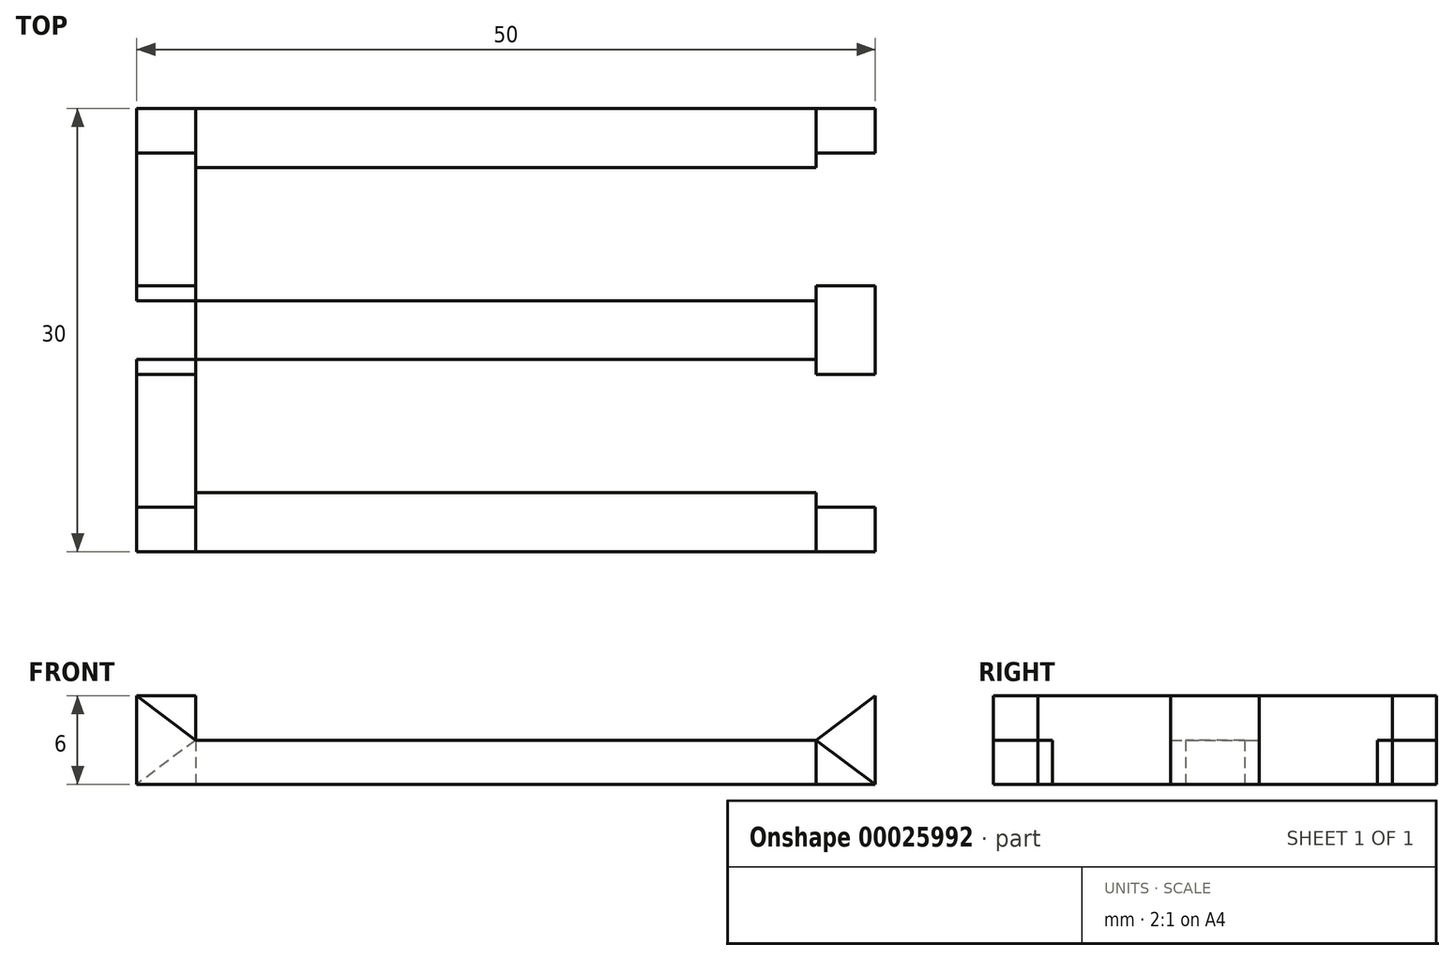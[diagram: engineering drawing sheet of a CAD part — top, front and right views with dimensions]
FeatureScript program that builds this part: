
annotation { "Feature Type Name" : "Feature", "Feature Type Description" : "" }
export const myFeature = defineFeature(function(context is Context, id is Id, definition is map)
    precondition{}
    {
        {
            var Q0;
            Q0=qCreatedBy(makeId("Top.planeOp"),FACE);
            cPlane(context, id + "F0", {"entities" : qUnion([Q0]), "cplaneType" : CPlaneType.OFFSET, "offset" : 3 * mm, "oppositeDirection" : true, "width" : 150 * mm, "height" : 150 * mm});
        }
        {
            var Q0;
            Q0=qCreatedBy(makeId("Top.planeOp"),FACE);
            var sketch = newSketch(context, id + "F1", { "sketchPlane" : qUnion([Q0])});
            skLineSegment(sketch, "E0", {"start": v(0, 0) * mm, "end": v(0, -19.58) * mm});
            skSolve(sketch);
        }
        {
            var Q0;
            Q0=qCreatedBy(id+"F0.planeOp",FACE);
            var sketch = newSketch(context, id + "F2", { "sketchPlane" : qUnion([Q0])});
            skLineSegment(sketch, "E1.rect.bottom", {"start": v(25, 15) * mm, "end": v(-25, 15) * mm});
            skLineSegment(sketch, "E1.rect.top", {"start": v(25, -15) * mm, "end": v(-25, -15) * mm});
            skLineSegment(sketch, "E1.rect.left", {"start": v(25, 15) * mm, "end": v(25, -15) * mm});
            skLineSegment(sketch, "E1.rect.right", {"start": v(-25, 15) * mm, "end": v(-25, -15) * mm});
            skPoint(sketch, "E1.rect.middle", {"position": v(0, 0) * mm});
            skLineSegment(sketch, "E2.0", {"start": v(25, 11) * mm, "end": v(-25, 11) * mm});
            skLineSegment(sketch, "E3.0", {"start": v(25, -11) * mm, "end": v(-25, -11) * mm});
            skLineSegment(sketch, "E4.0", {"start": v(-21, 15) * mm, "end": v(-21, -15) * mm});
            skLineSegment(sketch, "E5.0", {"start": v(21, 15) * mm, "end": v(21, -15) * mm});
            skLineSegment(sketch, "E6.rect.bottom", {"start": v(-25, 2) * mm, "end": v(25, 2) * mm});
            skLineSegment(sketch, "E6.rect.top", {"start": v(-25, -2) * mm, "end": v(25, -2) * mm});
            skLineSegment(sketch, "E6.rect.left", {"start": v(-25, 2) * mm, "end": v(-25, -2) * mm});
            skLineSegment(sketch, "E6.rect.right", {"start": v(25, 2) * mm, "end": v(25, -2) * mm});
            skSolve(sketch);
        }
        {
            var Q0;
            {var subQ3=sQuery(id+"F2.wireOp",EDGE,"E1.rect.right");var subQ6=sQuery(id+"F2.wireOp",EDGE,"E1.rect.top");var subQ8=makeQuery(id+"F2.imprint","INTERSECT",VERTEX,{"derivedFrom":[subQ6,subQ3]});Q0=makeQuery(id+"F2.imprint","IMPRINT",FACE,{"disambiguationData":[TD([[makeQuery(id+"F2.imprint","IMPRINT",EDGE,{"disambiguationData":[TD([[subQ8,1.0]])],"derivedFrom":subQ6}),-1.0]])]});}
            var Q1;
            {var subQ3=sQuery(id+"F2.wireOp",EDGE,"E1.rect.top");var subQ5=sQuery(id+"F2.wireOp",EDGE,"E4.0");var subQ7=makeQuery(id+"F2.imprint","INTERSECT",VERTEX,{"derivedFrom":[subQ3,subQ5]});Q1=makeQuery(id+"F2.imprint","IMPRINT",FACE,{"disambiguationData":[TD([[makeQuery(id+"F2.imprint","IMPRINT",EDGE,{"disambiguationData":[TD([[subQ7,1.0]])],"derivedFrom":subQ3}),-1.0]])]});}
            var Q2;
            {var subQ0=sQuery(id+"F2.wireOp",EDGE,"E6.rect.left");Q2=makeQuery(id+"F2.imprint","IMPRINT",FACE,{"disambiguationData":[TD([[makeQuery(id+"F2.imprint","IMPRINT",EDGE,{"derivedFrom":subQ0}),1.0]])]});}
            var Q3;
            {var subQ4=sQuery(id+"F2.wireOp",EDGE,"E1.rect.bottom");var subQ6=sQuery(id+"F2.wireOp",EDGE,"E1.rect.right");var subQ8=makeQuery(id+"F2.imprint","INTERSECT",VERTEX,{"derivedFrom":[subQ4,subQ6]});Q3=makeQuery(id+"F2.imprint","IMPRINT",FACE,{"disambiguationData":[TD([[makeQuery(id+"F2.imprint","IMPRINT",EDGE,{"disambiguationData":[TD([[subQ8,1.0]])],"derivedFrom":subQ4}),1.0]])]});}
            var Q4;
            {var subQ0=sQuery(id+"F2.wireOp",EDGE,"E4.0");var subQ3=sQuery(id+"F2.wireOp",EDGE,"E1.rect.bottom");var subQ4=makeQuery(id+"F2.imprint","INTERSECT",VERTEX,{"derivedFrom":[subQ3,subQ0]});Q4=makeQuery(id+"F2.imprint","IMPRINT",FACE,{"disambiguationData":[TD([[makeQuery(id+"F2.imprint","IMPRINT",EDGE,{"disambiguationData":[TD([[subQ4,1.0]])],"derivedFrom":subQ3}),1.0]])]});}
            var Q5;
            {var subQ3=sQuery(id+"F2.wireOp",EDGE,"E4.0");var subQ5=sQuery(id+"F2.wireOp",EDGE,"E6.rect.bottom");var subQ7=makeQuery(id+"F2.imprint","INTERSECT",VERTEX,{"derivedFrom":[subQ3,subQ5]});Q5=makeQuery(id+"F2.imprint","IMPRINT",FACE,{"disambiguationData":[TD([[makeQuery(id+"F2.imprint","IMPRINT",EDGE,{"disambiguationData":[TD([[subQ7,-1.0]])],"derivedFrom":subQ3}),1.0]])]});}
            var Q6;
            {var subQ3=sQuery(id+"F2.wireOp",EDGE,"E1.rect.right");var subQ5=sQuery(id+"F2.wireOp",EDGE,"E2.0");var subQ7=makeQuery(id+"F2.imprint","INTERSECT",VERTEX,{"derivedFrom":[subQ3,subQ5]});Q6=makeQuery(id+"F2.imprint","IMPRINT",FACE,{"disambiguationData":[TD([[makeQuery(id+"F2.imprint","IMPRINT",EDGE,{"disambiguationData":[TD([[subQ7,1.0]])],"derivedFrom":subQ5}),1.0]])]});}
            var Q7;
            {var subQ3=sQuery(id+"F2.wireOp",EDGE,"E1.rect.right");var subQ5=sQuery(id+"F2.wireOp",EDGE,"E3.0");var subQ7=makeQuery(id+"F2.imprint","INTERSECT",VERTEX,{"derivedFrom":[subQ3,subQ5]});Q7=makeQuery(id+"F2.imprint","IMPRINT",FACE,{"disambiguationData":[TD([[makeQuery(id+"F2.imprint","IMPRINT",EDGE,{"disambiguationData":[TD([[subQ7,1.0]])],"derivedFrom":subQ5}),-1.0]])]});}
            extrude(context, id + "F3", {"entities" : qUnion([Q0, Q1, Q2, Q3, Q4, Q5, Q6, Q7]), "depth" : 3 * mm});
        }
        {
            var Q0;
            {var subQ3=sQuery(id+"F2.wireOp",EDGE,"E1.rect.bottom");var subQ5=sQuery(id+"F2.wireOp",EDGE,"E1.rect.right");var subQ7=makeQuery(id+"F2.imprint","INTERSECT",VERTEX,{"derivedFrom":[subQ3,subQ5]});Q0=makeQuery(id+"F2.imprint","IMPRINT",FACE,{"disambiguationData":[TD([[makeQuery(id+"F2.imprint","IMPRINT",EDGE,{"disambiguationData":[TD([[subQ7,1.0]])],"derivedFrom":subQ3}),1.0]])]});}
            var Q1;
            {var subQ3=sQuery(id+"F2.wireOp",EDGE,"E1.rect.top");var subQ5=sQuery(id+"F2.wireOp",EDGE,"E1.rect.right");var subQ7=makeQuery(id+"F2.imprint","INTERSECT",VERTEX,{"derivedFrom":[subQ3,subQ5]});Q1=makeQuery(id+"F2.imprint","IMPRINT",FACE,{"disambiguationData":[TD([[makeQuery(id+"F2.imprint","IMPRINT",EDGE,{"disambiguationData":[TD([[subQ7,1.0]])],"derivedFrom":subQ3}),-1.0]])]});}
            var Q2;
            {var subQ3=sQuery(id+"F2.wireOp",EDGE,"E1.rect.right");var subQ5=sQuery(id+"F2.wireOp",EDGE,"E2.0");var subQ7=makeQuery(id+"F2.imprint","INTERSECT",VERTEX,{"derivedFrom":[subQ3,subQ5]});Q2=makeQuery(id+"F2.imprint","IMPRINT",FACE,{"disambiguationData":[TD([[makeQuery(id+"F2.imprint","IMPRINT",EDGE,{"disambiguationData":[TD([[subQ7,1.0]])],"derivedFrom":subQ5}),1.0]])]});}
            var Q3;
            {var subQ3=sQuery(id+"F2.wireOp",EDGE,"E1.rect.right");var subQ5=sQuery(id+"F2.wireOp",EDGE,"E3.0");var subQ7=makeQuery(id+"F2.imprint","INTERSECT",VERTEX,{"derivedFrom":[subQ3,subQ5]});Q3=makeQuery(id+"F2.imprint","IMPRINT",FACE,{"disambiguationData":[TD([[makeQuery(id+"F2.imprint","IMPRINT",EDGE,{"disambiguationData":[TD([[subQ7,1.0]])],"derivedFrom":subQ5}),-1.0]])]});}
            extrude(context, id + "F4", {"entities" : qUnion([Q0, Q1, Q2, Q3]), "operationType" : NewBodyOperationType.ADD, "depth" : 6 * mm});
        }
        {
            var Q0;
            Q0=qCreatedBy(makeId("Front.planeOp"),FACE);
            var sketch = newSketch(context, id + "F5", { "sketchPlane" : qUnion([Q0])});
            skLineSegment(sketch, "E7.bottom", {"start": v(25, -3) * mm, "end": v(21, -3) * mm});
            skLineSegment(sketch, "E7.top", {"start": v(25, 3) * mm, "end": v(21, 3) * mm});
            skLineSegment(sketch, "E7.left", {"start": v(25, -3) * mm, "end": v(25, 3) * mm});
            skLineSegment(sketch, "E7.right", {"start": v(21, -3) * mm, "end": v(21, 3) * mm});
            skLineSegment(sketch, "E8", {"start": v(21, 0) * mm, "end": v(25, 3) * mm});
            skSolve(sketch);
        }
        {
            var Q0;
            {var subQ2=sQuery(id+"F5.wireOp",EDGE,"E7.bottom");Q0=makeQuery(id+"F5.imprint","IMPRINT",FACE,{"disambiguationData":[TD([[makeQuery(id+"F5.imprint","IMPRINT",EDGE,{"derivedFrom":subQ2}),-1.0]])]});}
            extrude(context, id + "F6", {"entities" : qUnion([Q0]), "depth" : 3 * mm, "hasSecondDirection" : true, "secondDirectionOppositeDirection" : true, "secondDirectionDepth" : 3 * mm});
        }
        {
            var Q0;
            Q0=makeQuery(id+"F3.opExtrude","SWEPT_FACE",FACE,{"disambiguationData":[OSD([sQuery(id+"F2.wireOp",EDGE,"E1.rect.top")])]});
            var sketch = newSketch(context, id + "F7", { "sketchPlane" : qUnion([Q0])});
            skLineSegment(sketch, "E9", {"start": v(21, 0) * mm, "end": v(25, -3) * mm});
            skPoint(sketch, "E10.0", {"position": v(21, 0) * mm});
            skLineSegment(sketch, "E11", {"start": v(21, 0) * mm, "end": v(21, 0) * mm});
            skPoint(sketch, "E12.0", {"position": v(25, -3) * mm});
            skLineSegment(sketch, "E13", {"start": v(21, -3) * mm, "end": v(21, 0) * mm});
            skLineSegment(sketch, "E14", {"start": v(21, -3) * mm, "end": v(25, -3) * mm});
            skSolve(sketch);
        }
        {
            var Q0;
            Q0=makeQuery(id+"F7.imprint","IMPRINT",FACE,{"disambiguationData":[TD([[makeQuery(id+"F7.imprint","IMPRINT",EDGE,{"derivedFrom":sQuery(id+"F7.wireOp",EDGE,"E9")}),-1.0]])]});
            extrude(context, id + "F8", {"entities" : qUnion([Q0]), "oppositeDirection" : true, "depth" : 3 * mm});
        }
        {
            var Q0;
            Q0=makeQuery(id+"F3.opExtrude","SWEPT_FACE",FACE,{"disambiguationData":[OSD([sQuery(id+"F2.wireOp",EDGE,"E1.rect.bottom")])]});
            var sketch = newSketch(context, id + "F9", { "sketchPlane" : qUnion([Q0])});
            skPoint(sketch, "E15.0", {"position": v(-25, -3) * mm});
            skPoint(sketch, "E15.1", {"position": v(-21, 0) * mm});
            skPoint(sketch, "E15.2", {"position": v(-21, 0) * mm});
            skLineSegment(sketch, "E16.4", {"start": v(-21, 0) * mm, "end": v(-25, -3) * mm});
            skLineSegment(sketch, "E17", {"start": v(-21, -3) * mm, "end": v(-25, -3) * mm});
            skLineSegment(sketch, "E18", {"start": v(-21, -3) * mm, "end": v(-21, 0) * mm});
            skSolve(sketch);
        }
        {
            var Q0;
            Q0=makeQuery(id+"F9.imprint","IMPRINT",FACE,{"disambiguationData":[TD([[makeQuery(id+"F9.imprint","IMPRINT",EDGE,{"derivedFrom":sQuery(id+"F9.wireOp",EDGE,"E16.4")}),1.0]])]});
            extrude(context, id + "F10", {"entities" : qUnion([Q0]), "oppositeDirection" : true, "depth" : 3 * mm});
        }
        {
            var Q0;
            Q0=makeQuery(id+"F6.opExtrude","SWEPT_BODY",BODY,{"disambiguationData":[OSD([sQuery(id+"F5.wireOp",EDGE,"E7.bottom"),sQuery(id+"F5.wireOp",EDGE,"E7.left"),sQuery(id+"F5.wireOp",EDGE,"E7.right"),sQuery(id+"F5.wireOp",EDGE,"E8")])]});
            var Q1;
            Q1=makeQuery(id+"F8.opExtrude","SWEPT_BODY",BODY,{"disambiguationData":[OSD([sQuery(id+"F7.wireOp",EDGE,"E9"),sQuery(id+"F7.wireOp",EDGE,"E13"),sQuery(id+"F7.wireOp",EDGE,"E14")])]});
            var Q2;
            Q2=makeQuery(id+"F10.opExtrude","SWEPT_BODY",BODY,{"disambiguationData":[OSD([sQuery(id+"F9.wireOp",EDGE,"E16.4"),sQuery(id+"F9.wireOp",EDGE,"E17"),sQuery(id+"F9.wireOp",EDGE,"E18")])]});
            var Q3;
            Q3=sQuery(id+"F1.wireOp",EDGE,"E0");
            transform(context, id + "F11", {"entities" : qUnion([Q0, Q1, Q2]), "transformType" : TransformType.ROTATION, "transformAxis" : qUnion([Q3]), "angle" : 180 * degree, "makeCopy" : true});
        }
        {
            var Q0;
            Q0=makeQuery(id+"F11.opPattern","COPY",BODY,{"derivedFrom":makeQuery(id+"F6.opExtrude","SWEPT_BODY",BODY,{"disambiguationData":[OSD([sQuery(id+"F5.wireOp",EDGE,"E7.bottom"),sQuery(id+"F5.wireOp",EDGE,"E7.left"),sQuery(id+"F5.wireOp",EDGE,"E7.right"),sQuery(id+"F5.wireOp",EDGE,"E8")])]}),"instanceName":"1"});
            var Q1;
            Q1=makeQuery(id+"F11.opPattern","COPY",BODY,{"derivedFrom":makeQuery(id+"F8.opExtrude","SWEPT_BODY",BODY,{"disambiguationData":[OSD([sQuery(id+"F7.wireOp",EDGE,"E9"),sQuery(id+"F7.wireOp",EDGE,"E13"),sQuery(id+"F7.wireOp",EDGE,"E14")])]}),"instanceName":"1"});
            var Q2;
            Q2=makeQuery(id+"F11.opPattern","COPY",BODY,{"derivedFrom":makeQuery(id+"F10.opExtrude","SWEPT_BODY",BODY,{"disambiguationData":[OSD([sQuery(id+"F9.wireOp",EDGE,"E16.4"),sQuery(id+"F9.wireOp",EDGE,"E17"),sQuery(id+"F9.wireOp",EDGE,"E18")])]}),"instanceName":"1"});
            var Q3;
            Q3=makeQuery(id+"F3.opExtrude","SWEPT_BODY",BODY,{"disambiguationData":[OSD([sQuery(id+"F2.wireOp",EDGE,"E1.rect.bottom"),sQuery(id+"F2.wireOp",EDGE,"E1.rect.top"),sQuery(id+"F2.wireOp",EDGE,"E1.rect.right"),sQuery(id+"F2.wireOp",EDGE,"E2.0"),sQuery(id+"F2.wireOp",EDGE,"E3.0"),sQuery(id+"F2.wireOp",EDGE,"E4.0"),sQuery(id+"F2.wireOp",EDGE,"E5.0"),sQuery(id+"F2.wireOp",EDGE,"E6.rect.bottom"),sQuery(id+"F2.wireOp",EDGE,"E6.rect.top"),sQuery(id+"F2.wireOp",EDGE,"E6.rect.left")])]});
            booleanBodies(context, id + "F12", {"operationType" : BooleanOperationType.SUBTRACTION, "tools" : qUnion([Q0, Q1, Q2]), "targets" : qUnion([Q3])});
        }
    });
